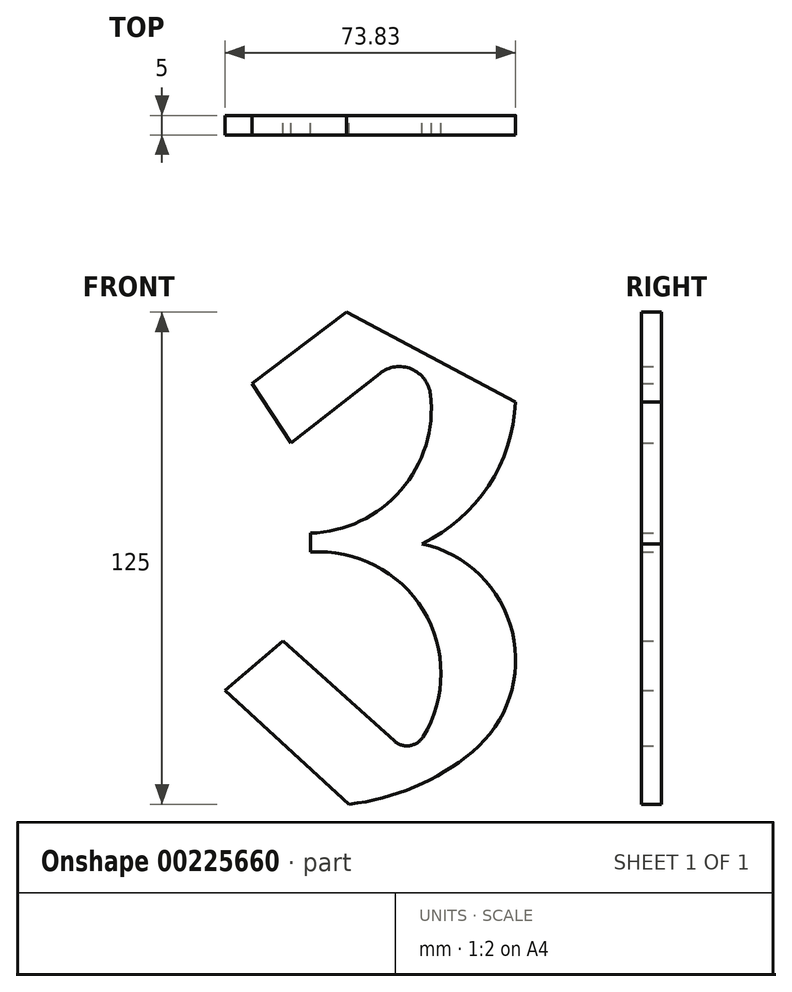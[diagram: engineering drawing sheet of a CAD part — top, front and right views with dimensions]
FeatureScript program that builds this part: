
annotation { "Feature Type Name" : "Feature", "Feature Type Description" : "" }
export const myFeature = defineFeature(function(context is Context, id is Id, definition is map)
    precondition{}
    {
        {
            var Q0;
            Q0=qCreatedBy(makeId("Front.planeOp"),FACE);
            var sketch = newSketch(context, id + "F0", { "sketchPlane" : qUnion([Q0])});
            skLineSegment(sketch, "E0", {"start": v(29.57, 14.12) * mm, "end": v(-1.88, 42.96) * mm});
            skLineSegment(sketch, "E1", {"start": v(-1.88, 42.96) * mm, "end": v(12.9, 55.56) * mm});
            skLineSegment(sketch, "E2", {"start": v(12.9, 55.56) * mm, "end": v(41.12, 30.15) * mm});
            skPoint(sketch, "E3", {"position": v(22.05, 47.32) * mm});
            skArc(sketch, "E4", {"start": v(48.43, 31.21) * mm, "mid": v(48.44, 63.4) * mm, "end": v(19.83, 78.15) * mm});
            skLineSegment(sketch, "E5", {"start": v(19.83, 78.15) * mm, "end": v(19.83, 82.97) * mm});
            skPoint(sketch, "E6", {"position": v(18.87, 114.62) * mm});
            skArc(sketch, "E7", {"start": v(19.83, 82.97) * mm, "mid": v(42.8, 93.9) * mm, "end": v(50.33, 118.19) * mm});
            skLineSegment(sketch, "E8", {"start": v(37.43, 123.57) * mm, "end": v(14.93, 105.86) * mm});
            skLineSegment(sketch, "E9", {"start": v(14.93, 105.86) * mm, "end": v(4.94, 121) * mm});
            skLineSegment(sketch, "E10", {"start": v(4.94, 121) * mm, "end": v(28.94, 139.12) * mm});
            skLineSegment(sketch, "E11", {"start": v(28.94, 139.12) * mm, "end": v(71.86, 116.33) * mm});
            skArc(sketch, "E12", {"start": v(50.33, 118.19) * mm, "mid": v(45.46, 124.67) * mm, "end": v(37.43, 123.57) * mm});
            skPoint(sketch, "E13", {"position": v(30.2, 117.88) * mm});
            skArc(sketch, "E14", {"start": v(71.86, 116.33) * mm, "mid": v(65.05, 95) * mm, "end": v(48.2, 80.28) * mm});
            skPoint(sketch, "E15", {"position": v(38.37, 47.13) * mm});
            skArc(sketch, "E16", {"start": v(60.98, 27.42) * mm, "mid": v(71.1, 57.84) * mm, "end": v(48.2, 80.28) * mm});
            skPoint(sketch, "E17", {"position": v(158.99, 76.01) * mm});
            skArc(sketch, "E18", {"start": v(134.7, 15.2) * mm, "mid": v(99.99, 47.58) * mm, "end": v(96.27, 94.9) * mm});
            skPoint(sketch, "E19", {"position": v(175.56, 71.02) * mm});
            skArc(sketch, "E20", {"start": v(96.27, 94.9) * mm, "mid": v(108.42, 119.49) * mm, "end": v(127.93, 138.76) * mm});
            skLineSegment(sketch, "E21", {"start": v(127.93, 138.76) * mm, "end": v(157.23, 126.1) * mm});
            skLineSegment(sketch, "E22", {"start": v(157.23, 126.1) * mm, "end": v(147.46, 108.73) * mm});
            skLineSegment(sketch, "E23", {"start": v(147.46, 108.73) * mm, "end": v(119.25, 121.4) * mm});
            skPoint(sketch, "E24", {"position": v(158.33, 86.93) * mm});
            skArc(sketch, "E25", {"start": v(119.25, 121.4) * mm, "mid": v(107.34, 97.69) * mm, "end": v(108.66, 71.19) * mm});
            skPoint(sketch, "E26", {"position": v(131.4, 53.86) * mm});
            skArc(sketch, "E27", {"start": v(151, 35.34) * mm, "mid": v(156.55, 63.6) * mm, "end": v(133.42, 80.76) * mm});
            skLineSegment(sketch, "E28", {"start": v(111.06, 65) * mm, "end": v(133.42, 80.76) * mm});
            skLineSegment(sketch, "E29", {"start": v(108.66, 71.19) * mm, "end": v(144.93, 97.88) * mm});
            skPoint(sketch, "E30", {"position": v(135.71, 63.09) * mm});
            skArc(sketch, "E31", {"start": v(144.93, 97.88) * mm, "mid": v(169.85, 74.51) * mm, "end": v(164.02, 40.86) * mm});
            skArc(sketch, "E32", {"start": v(48.43, 31.21) * mm, "mid": v(45.03, 28.97) * mm, "end": v(41.12, 30.15) * mm});
            skArc(sketch, "E33", {"start": v(60.98, 27.42) * mm, "mid": v(46.25, 18.47) * mm, "end": v(29.57, 14.12) * mm});
            skArc(sketch, "E34", {"start": v(164.02, 40.86) * mm, "mid": v(150.56, 26.65) * mm, "end": v(134.7, 15.2) * mm});
            skArc(sketch, "E35.trimOffspring", {"start": v(111.06, 65) * mm, "mid": v(127.27, 45.1) * mm, "end": v(151, 35.34) * mm});
            skSolve(sketch);
        }
        {
            var Q0;
            Q0=makeQuery(id+"F0.imprint","IMPRINT",FACE,{"disambiguationData":[TD([[makeQuery(id+"F0.imprint","IMPRINT",EDGE,{"derivedFrom":sQuery(id+"F0.wireOp",EDGE,"E0")}),-1.0]])]});
            var Q1;
            Q1=makeQuery(id+"F0.imprint","IMPRINT",FACE,{"disambiguationData":[TD([[makeQuery(id+"F0.imprint","IMPRINT",EDGE,{"derivedFrom":sQuery(id+"F0.wireOp",EDGE,"E18")}),-1.0]])]});
            extrude(context, id + "F1", {"entities" : qUnion([Q0, Q1]), "depth" : 5 * mm});
        }
    });
